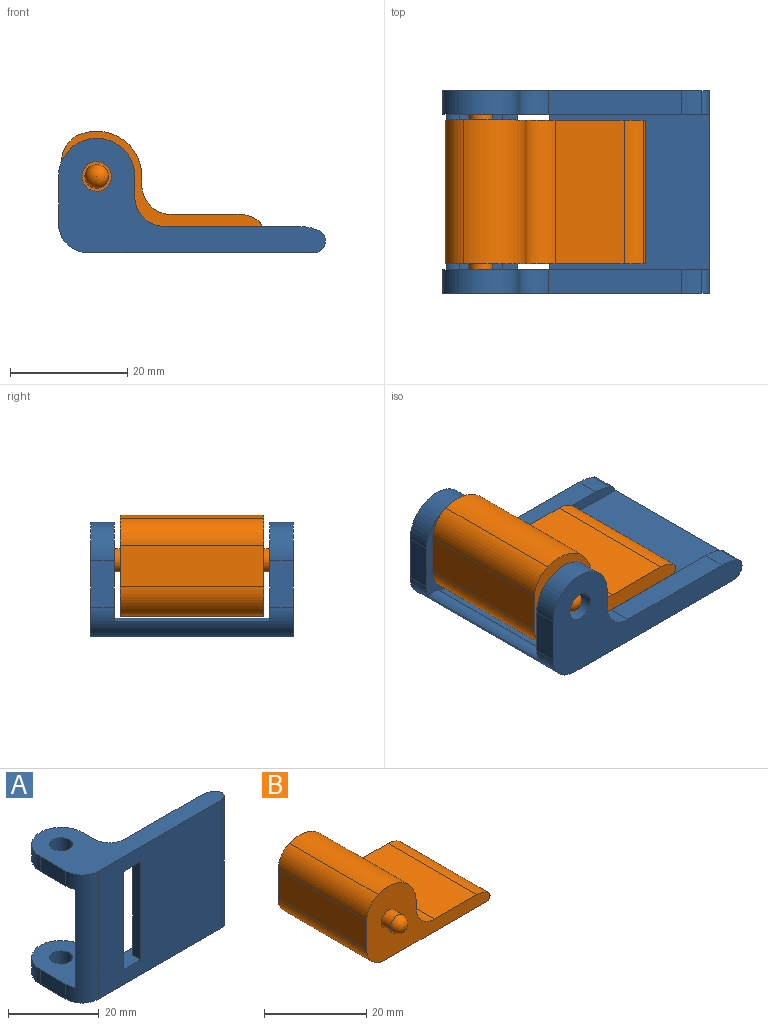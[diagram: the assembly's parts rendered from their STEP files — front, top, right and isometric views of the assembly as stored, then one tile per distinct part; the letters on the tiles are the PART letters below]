
ASSEMBLY  parts=2 mates=1
PART A: 27 faces, bbox 45.5x19.5x34.5 mm
  f0: plane 8x4mm, normal (-1,0,0), area 32mm2, adj f1,f17,f19,f26
  f1: plane 45.41x19.5mm, normal (0,0,1), area 266.1mm2, adj f0,f2,f3,f13,f14,f15,f16,f17
  f2: plane 26.5x5.28mm, normal (0,1,0), area 139.9mm2, adj f1,f12,f23,f24
  f3: plane 38.47x34.5mm, normal (0,-1,0), area 1181.6mm2, adj f1,f11,f12,f19,f21,f22,f23,f26
  f4: cylinder r=10mm len=4mm, axis (0,0,-1), area 14.2mm2, adj f5,f11,f12,f21
  f5: plane 22.69x4mm, normal (0,1,0), area 90.8mm2, adj f4,f6,f11,f12
  f6: cylinder r=5mm len=5mm, axis (0,0,-1), area 31.4mm2, adj f5,f7,f11,f12
  f7: plane 4x3.5mm, normal (1,0,0), area 14mm2, adj f6,f8,f11,f12
  f8: cylinder r=6.5mm len=13mm, axis (0,0,-1), area 81.7mm2, adj f7,f9,f11,f12
  f9: plane 8x4mm, normal (-1,0,0), area 32mm2, adj f8,f11,f12,f26
  f10: cylinder r=2.5mm len=5mm, axis (0,0,-1), area 62.8mm2, adj f11,f12
  f11: plane 45.47x19.5mm, normal (0,0,1), area 358.8mm2, adj f3,f4,f5,f6,f7,f8,f9,f10
  f12: plane 45.41x19.5mm, normal (0,0,-1), area 266.1mm2, adj f2,f3,f4,f5,f6,f7,f8,f9
  f13: plane 27.13x26.5mm, normal (0,1,0), area 719mm2, adj f1,f12,f21,f22
  f14: plane 22.69x4mm, normal (0,1,0), area 90.8mm2, adj f1,f15,f19,f20
  f15: cylinder r=5mm len=5mm, axis (0,0,1), area 31.4mm2, adj f1,f14,f16,f19
  f16: plane 4x3.5mm, normal (1,0,0), area 14mm2, adj f1,f15,f17,f19
  f17: cylinder r=6.5mm len=13mm, axis (0,0,1), area 81.7mm2, adj f0,f1,f16,f19
  f18: cylinder r=2.5mm len=5mm, axis (0,0,1), area 62.8mm2, adj f1,f19
  f19: plane 45.47x19.5mm, normal (0,0,-1), area 358.8mm2, adj f0,f3,f14,f15,f16,f17,f18,f20
  f20: cylinder r=10mm len=4mm, axis (0,0,-1), area 14.2mm2, adj f1,f14,f19,f21
  f21: cylinder r=2mm len=34.5mm, axis (0,0,-1), area 141.2mm2, adj f1,f3,f4,f11,f12,f13,f19,f20
  f22: plane 26.5x2.5mm, normal (-1,0,0), area 66.2mm2, adj f1,f3,f12,f13
  f23: plane 26.5x2.5mm, normal (0.71,0.71,0), area 93.7mm2, adj f1,f2,f3,f12
  f24: cylinder r=5mm len=26.5mm, axis (0,0,-1), area 58.7mm2, adj f1,f2,f12,f25
  f25: cylinder r=2mm len=26.5mm, axis (0,0,-1), area 64.3mm2, adj f1,f12,f24,f26
  f26: cylinder r=5mm len=34.5mm, axis (0,0,-1), area 205mm2, adj f0,f1,f3,f9,f11,f12,f19,f25
PART B: 19 faces, bbox 34.1x33.5x17.2 mm
  f0: plane 24.5x6.99mm, normal (-1,0,0), area 171.3mm2, adj f5,f6,f9,f13
  f1: plane 28.06x24.5mm, normal (0,0,-1), area 687.5mm2, adj f5,f6,f13,f15
  f2: plane 24.5x11.73mm, normal (0,0,1), area 287.3mm2, adj f5,f6,f10,f14
  f3: plane 24.5x1.96mm, normal (1,0,0), area 48mm2, adj f4,f5,f6,f14
  f4: cylinder r=7.7mm len=24.5mm, axis (0,1,0), area 356.2mm2, adj f3,f5,f6,f9
  f5: plane 34.06x17.19mm, normal (0,-1,0), area 262.9mm2, adj f0,f1,f2,f3,f4,f7,f9,f10
  f6: plane 34.06x17.19mm, normal (0,1,0), area 262.9mm2, adj f0,f1,f2,f3,f4,f8,f9,f10
  f7: cylinder r=2mm len=4mm, axis (0,1,0), area 31.4mm2, adj f5,f12
  f8: cylinder r=2mm len=4mm, axis (0,1,0), area 31.4mm2, adj f6,f11
  f9: cylinder r=5mm len=24.5mm, axis (0,1,0), area 146mm2, adj f0,f4,f5,f6
  f10: cylinder r=5mm len=24.5mm, axis (0,1,0), area 88.5mm2, adj f2,f5,f6,f15
  f11: sphere r=2mm, area 25.1mm2, adj f8
  f12: sphere r=2mm, area 25.1mm2, adj f7
  f13: cylinder r=5mm len=24.5mm, axis (0,-1,0), area 192.4mm2, adj f0,f1,f5,f6
  f14: cylinder r=5mm len=24.5mm, axis (0,1,0), area 192.4mm2, adj f2,f3,f5,f6
  f15: cylinder r=1mm len=24.5mm, axis (0,1,0), area 59.3mm2, adj f1,f5,f6,f10
  f16: plane 4x4mm, normal (0,1,0), area 12.6mm2, adj f17
  f17: cylinder r=2mm len=15.5mm, axis (0,1,0), area 194.8mm2, adj f16,f18
  f18: plane 4x4mm, normal (0,-1,0), area 12.6mm2, adj f17
PLACE A rot(axis=(1,0,0),90deg) t=(-27.5,-56.85,26.26)mm
PLACE B t=(-17.5,-32.35,16.78)mm
MATE revolute B.f4 <-> A.f10  axis (0,-1,0) through (-27.5,-56.85,26.26)mm
